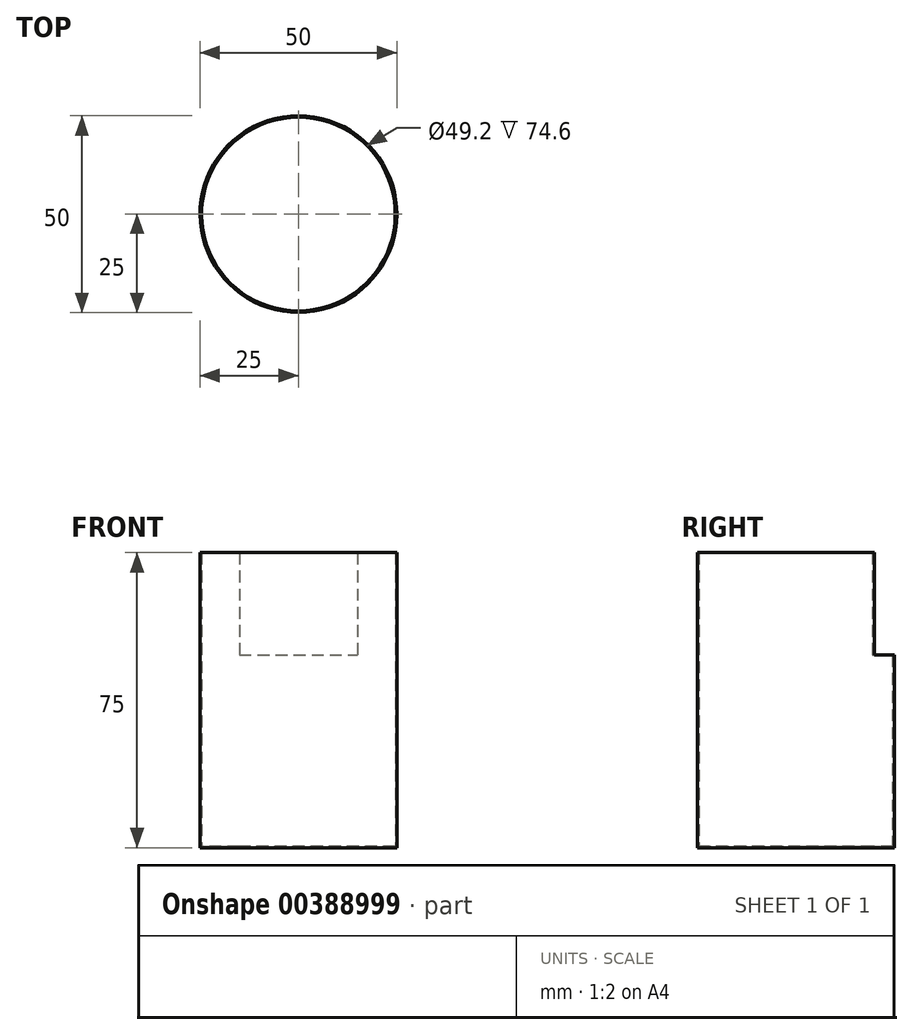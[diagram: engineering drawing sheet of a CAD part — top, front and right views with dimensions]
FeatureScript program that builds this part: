
annotation { "Feature Type Name" : "Feature", "Feature Type Description" : "" }
export const myFeature = defineFeature(function(context is Context, id is Id, definition is map)
    precondition{}
    {
        {
            var Q0;
            Q0=qCreatedBy(makeId("Top.planeOp"),FACE);
            var sketch = newSketch(context, id + "F0", { "sketchPlane" : qUnion([Q0])});
            skCircle(sketch, "E0", {"center": v(0, 0) * mm, "radius": 25 * mm});
            skSolve(sketch);
        }
        {
            var Q0;
            Q0=makeQuery(id+"F0.imprint","IMPRINT",FACE,{"disambiguationData":[TD([[makeQuery(id+"F0.imprint","IMPRINT",EDGE,{"derivedFrom":sQuery(id+"F0.wireOp",EDGE,"E0")}),1.0]])]});
            extrude(context, id + "F1", {"entities" : qUnion([Q0]), "depth" : 75 * mm});
        }
        {
            var Q0;
            Q0=makeQuery(id+"F1.opExtrude","CAP_FACE",FACE,{"disambiguationData":[OSD([sQuery(id+"F0.wireOp",EDGE,"E0")])],"isStart":false});
            shell(context, id + "F2", {"entities" : qUnion([Q0]), "thickness" : 0.4 * mm});
        }
        {
            var Q0;
            Q0=qCreatedBy(makeId("Front.planeOp"),FACE);
            var sketch = newSketch(context, id + "F3", { "sketchPlane" : qUnion([Q0])});
            skLineSegment(sketch, "E1.bottom", {"start": v(-15, 75) * mm, "end": v(15, 75) * mm});
            skLineSegment(sketch, "E1.top", {"start": v(-15, 49) * mm, "end": v(15, 49) * mm});
            skLineSegment(sketch, "E1.left", {"start": v(-15, 75) * mm, "end": v(-15, 49) * mm});
            skLineSegment(sketch, "E1.right", {"start": v(15, 75) * mm, "end": v(15, 49) * mm});
            skSolve(sketch);
        }
        {
            var Q0;
            Q0=makeQuery(id+"F3.imprint","IMPRINT",FACE,{"disambiguationData":[TD([[makeQuery(id+"F3.imprint","IMPRINT",EDGE,{"derivedFrom":sQuery(id+"F3.wireOp",EDGE,"E1.bottom")}),-1.0]])]});
            extrude(context, id + "F4", {"entities" : qUnion([Q0]), "operationType" : NewBodyOperationType.REMOVE, "endBound" : BoundingType.THROUGH_ALL, "oppositeDirection" : true, "depth" : 25 * mm});
        }
    });
